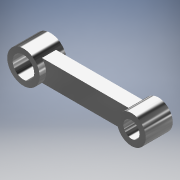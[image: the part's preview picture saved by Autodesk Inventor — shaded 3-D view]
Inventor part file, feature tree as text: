
AUTODESK INVENTOR PART (.ipt)
format: ipt  version: 2018.1 (Build 221171000, 171)  size: 134,144 bytes
history: native  units: in
note: dims shown in document units (in); Inventor stores cm internally (conversion verified against a paired STEP export)
features: extrude x2, sketch x2, mirror x1, plane x1
ambient origin geometry x8: Origin, YZ Plane, XZ Plane, XY Plane, X Axis, Y Axis, Z Axis, Center Point
bodies: Solid1 (feature_tree)
feature tree (6):
  extrude  "Extrusion1"  Depth=0.0472in TaperAngle=0.0deg
  extrude  "Extrusion2"  [1 undecoded]
  mirror  "Mirror1"
  sketch  "Sketch1"  dims[d7=0.1024in d8=0.0in d9=0.0472in d10=0.0in]
  sketch  "Sketch2"
  plane  "Work Plane1"
note: 1 required parameter value undecoded (feature->parameter linkage not recoverable at this tier; creation-order binding heuristic only, values carry confidence <= 0.55)
